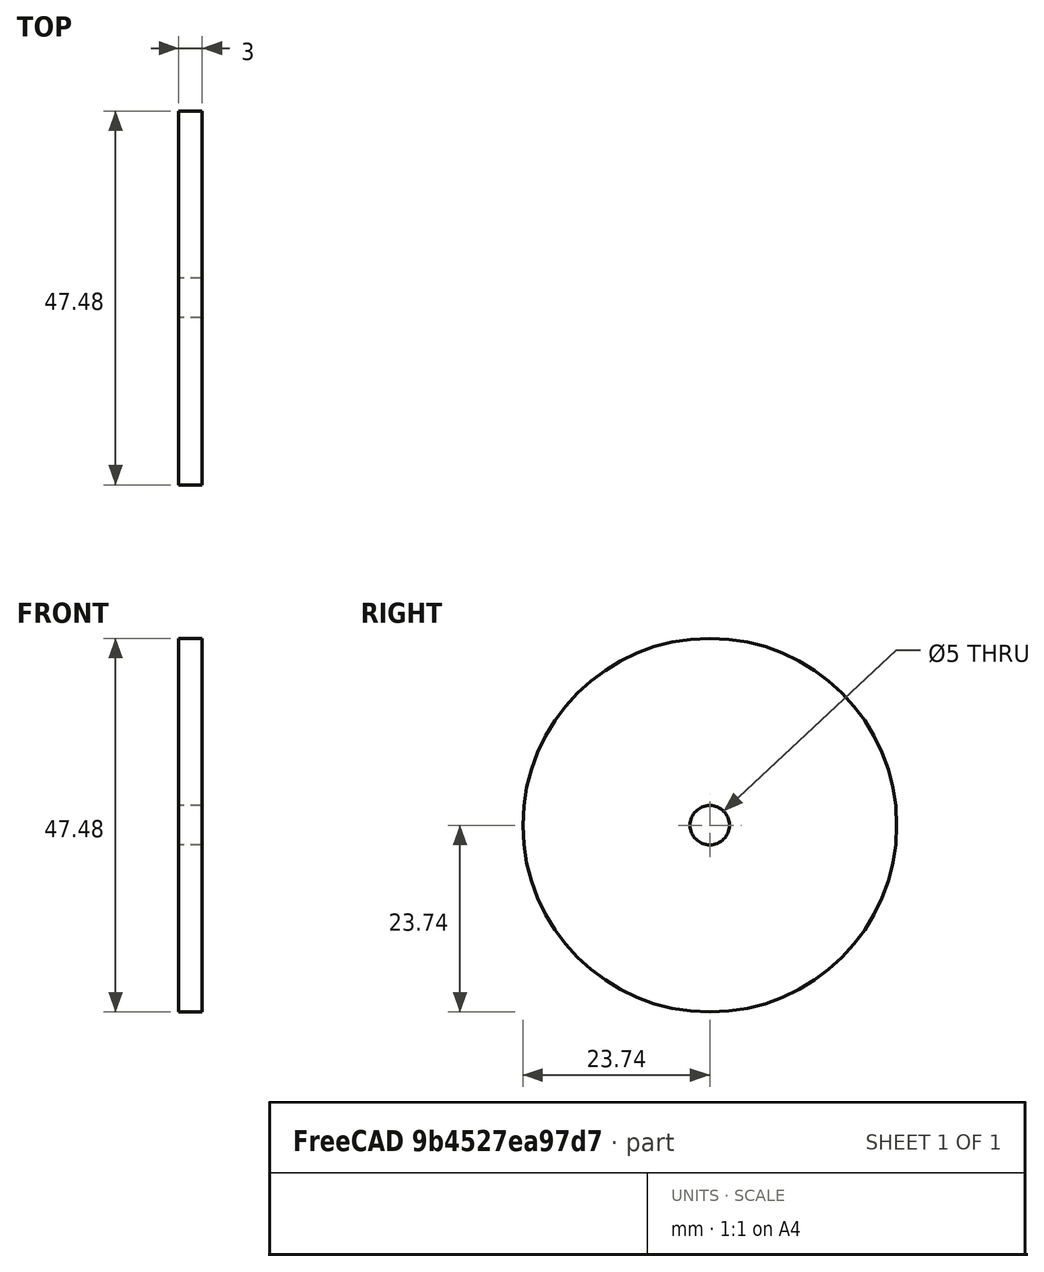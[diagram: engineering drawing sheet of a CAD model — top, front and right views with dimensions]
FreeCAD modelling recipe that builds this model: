
FCSTD DOCUMENT  (FreeCAD 0.18R16110 (Git))
Label: centergabarit
License: All rights reserved
LicenseURL: http://en.wikipedia.org/wiki/All_rights_reserved
objects: Sketcher::SketchObject×1, Part::Revolution×1
note: 2 computed .brp shape members not serialized (recipe doc carries the construction recipe); baked Part::Feature solids carry a one-line shape summary decoded from their .brp

FEATURE [Sketcher::SketchObject] Sketch
  sketch-geometry (4):
    g0: LineSegment StartX=-1.5 StartY=23.74 StartZ=0 EndX=1.5 EndY=23.74 EndZ=0
    g1: LineSegment StartX=1.5 StartY=23.74 StartZ=0 EndX=1.5 EndY=2.5 EndZ=0
    g2: LineSegment StartX=1.5 StartY=2.5 StartZ=0 EndX=-1.5 EndY=2.5 EndZ=0
    g3: LineSegment StartX=-1.5 StartY=2.5 StartZ=0 EndX=-1.5 EndY=23.74 EndZ=0
  constraints (11):
    c: Coincident(g0,g1)
    c: Coincident(g1,g2)
    c: Coincident(g2,g3)
    c: Coincident(g3,g0)
    c: Horizontal(g0)
    c: Vertical(g1)
    c: Vertical(g3)
    c: DistanceY(g0) = 23.74
    c: DistanceY(g1) = 2.5
    c: Distance(g0) = 3
    c: Symmetric(g2,g1,g-2)
FEATURE [Part::Revolution] Revolve
  Angle = 360
  Axis = (1,0,0)
  Base = (0,0,0)
  FaceMakerClass = Part::FaceMakerBullseye
  Solid = false
  Source = -> Sketch
  Symmetric = false
